# Revit family: Sensor-Lutron-Ceiling-Radio_Powr_Savr-Wireless_Occupancy_and_Vacancy-LRF2-OCR2B-P-WH
name_source: partatom
category: Lighting Devices
units: mm (PartAtom-declared; Revit-internal decimal feet)

## family parameters
Cut with Voids When Loaded = No
Host = Face
Maintain Annotation Orientation = Yes
OmniClass Number = 23.85.80.11.27
OmniClass Title = Lighting Controls
Part Type = Normal
Room Calculation Point = No
Round Connector Dimension = Use Diameter
Shared = No

## types (1)
- LRF2-OCR2B-P-WH
    Assembly Code = D5030800
    Cost = 0 $
    Coverage = 676.00 SF
    Coverage Area = 360˚ coverage ranges from 324 ft2 (30.2 m2) to 676 ft2 (62.4 m2), depending on mounting height
    Default Elevation = 0' - 0"
    Depth = 0' - 1 17/128"
    Description = Dual Technology Ceiling Mount Occupancy Sensor
    Field of View = 360.00°
    Finish = Plastic - Lutron - White Gloss
    Instruction Sheet Link = https://assets.lutron.com
    Keynote = 16500
    Length = 0' - 3 73/128"
    Manufacturer = Lutron Electronics Co., Inc
    Manufacturer Fax Number = 610-282-1243
    Maximum Operating Temperature = 104 °F
    Model = LRF2-OCR2B-P-WH
    Performance URL = https://www.lutron.com
    Product Documentation Link = https://assets.lutron.com
    Product Name = Radio Powr Savr Wireless Occupancy Sensor
    Product Page URL = https://www.lutron.com
    Sensor Material = Plastic - Lutron - White Gloss
    Sensor Type = Occupancy/Vacancy
    Series = Radio Powr Savr
    URL = http://www.lutron.com
    Version = 2021 - v1.0a
    Video Link = https://www.youtube.com
    Voltage = 3 V
    Voltage Comments = Operating voltage: 3 V
    Warranty URL = https://www.lutron.com
    Width = 0' - 3 73/128"

## geometry (parser evidence)
native form markers: Sweep x4
no freeform markers — native parametric forms only
